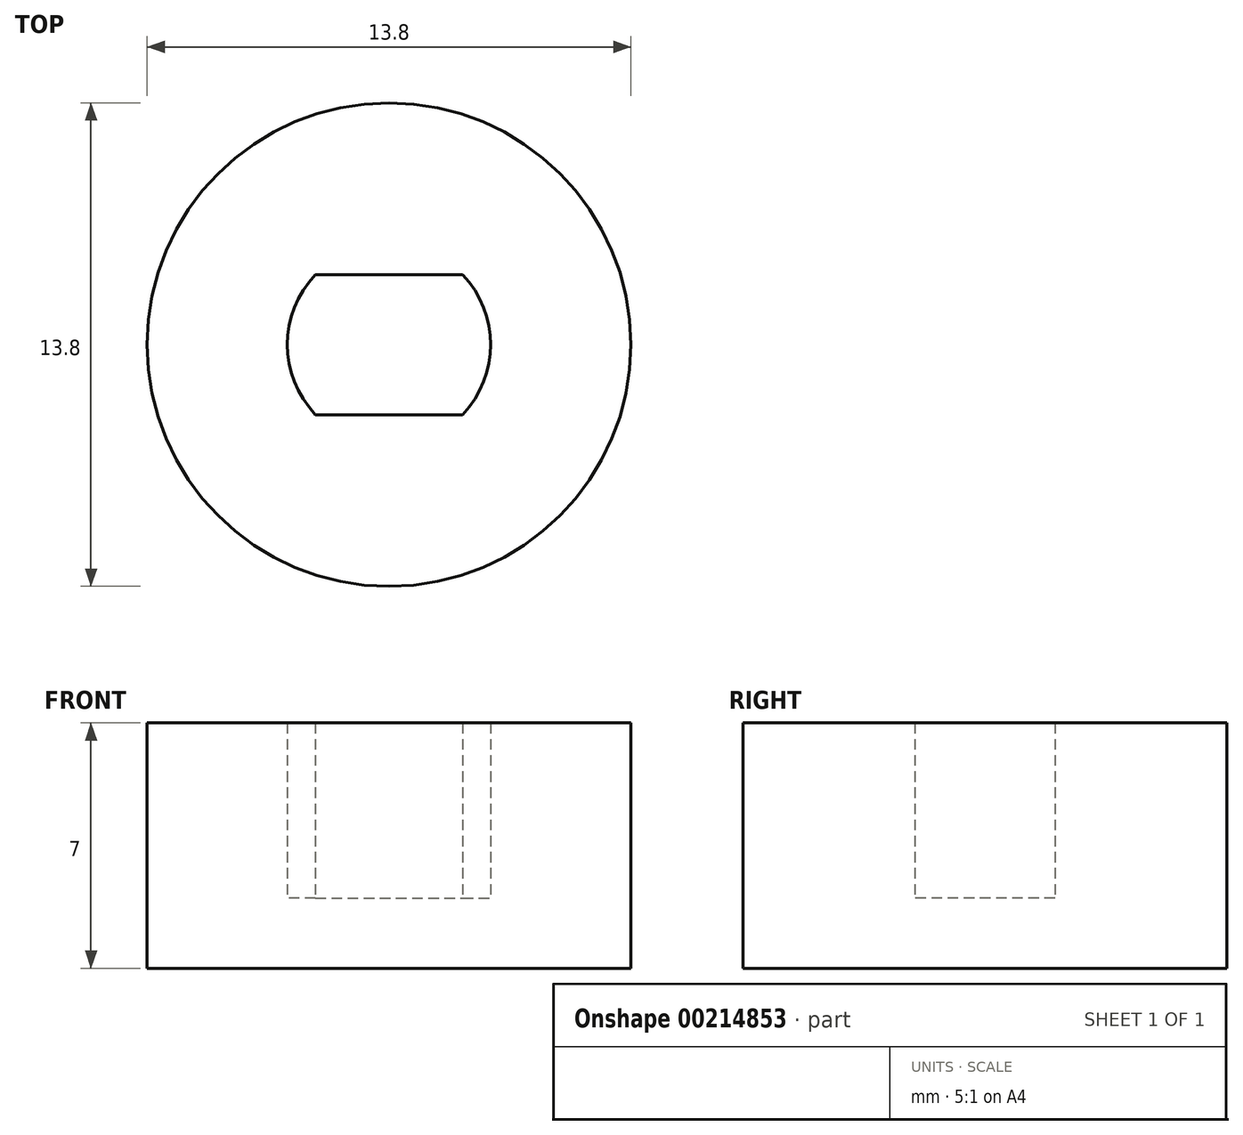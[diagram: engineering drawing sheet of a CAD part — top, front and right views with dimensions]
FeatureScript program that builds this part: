
annotation { "Feature Type Name" : "Feature", "Feature Type Description" : "" }
export const myFeature = defineFeature(function(context is Context, id is Id, definition is map)
    precondition{}
    {
        {
            var Q0;
            Q0=qCreatedBy(makeId("Top.planeOp"),FACE);
            var sketch = newSketch(context, id + "F0", { "sketchPlane" : qUnion([Q0])});
            skArc(sketch, "E0", {"start": v(-2.1, 2) * mm, "mid": v(-2.9, 0) * mm, "end": v(-2.1, -2) * mm, "construction": true});
            skLineSegment(sketch, "E1", {"start": v(-2.1, 2) * mm, "end": v(2.1, 2) * mm, "construction": true});
            skLineSegment(sketch, "E2.MirrorCS", {"start": v(-2.1, -2) * mm, "end": v(2.1, -2) * mm, "construction": true});
            skCircle(sketch, "E3", {"center": v(0, 0) * mm, "radius": 6.9 * mm});
            skArc(sketch, "E4.trimOffspring", {"start": v(2.1, -2) * mm, "mid": v(2.9, 0) * mm, "end": v(2.1, 2) * mm, "construction": true});
            skSolve(sketch);
        }
        {
            var Q0;
            Q0=qCreatedBy(makeId("Top.planeOp"),FACE);
            var sketch = newSketch(context, id + "F1", { "sketchPlane" : qUnion([Q0])});
            skCircle(sketch, "E5.0", {"center": v(0, 0) * mm, "radius": 6.9 * mm});
            skLineSegment(sketch, "E6.0", {"start": v(-2.1, -2) * mm, "end": v(2.1, -2) * mm});
            skArc(sketch, "E7.0", {"start": v(-2.1, 2) * mm, "mid": v(-2.9, 0) * mm, "end": v(-2.1, -2) * mm});
            skLineSegment(sketch, "E8.0", {"start": v(-2.1, 2) * mm, "end": v(2.1, 2) * mm});
            skArc(sketch, "E9.0", {"start": v(2.1, -2) * mm, "mid": v(2.9, 0) * mm, "end": v(2.1, 2) * mm});
            skSolve(sketch);
        }
        {
            var Q0;
            Q0=makeQuery(id+"F0.imprint","IMPRINT",FACE,{"disambiguationData":[TD([[makeQuery(id+"F0.imprint","IMPRINT",EDGE,{"derivedFrom":sQuery(id+"F0.wireOp",EDGE,"E3")}),1.0]])]});
            extrude(context, id + "F2", {"entities" : qUnion([Q0]), "oppositeDirection" : true, "depth" : 2 * mm});
        }
        {
            var Q0;
            Q0=makeQuery(id+"F1.imprint","IMPRINT",FACE,{"disambiguationData":[TD([[makeQuery(id+"F1.imprint","IMPRINT",EDGE,{"derivedFrom":sQuery(id+"F1.wireOp",EDGE,"E5.0")}),1.0]])]});
            extrude(context, id + "F3", {"entities" : qUnion([Q0]), "operationType" : NewBodyOperationType.ADD, "depth" : 5 * mm});
        }
    });
